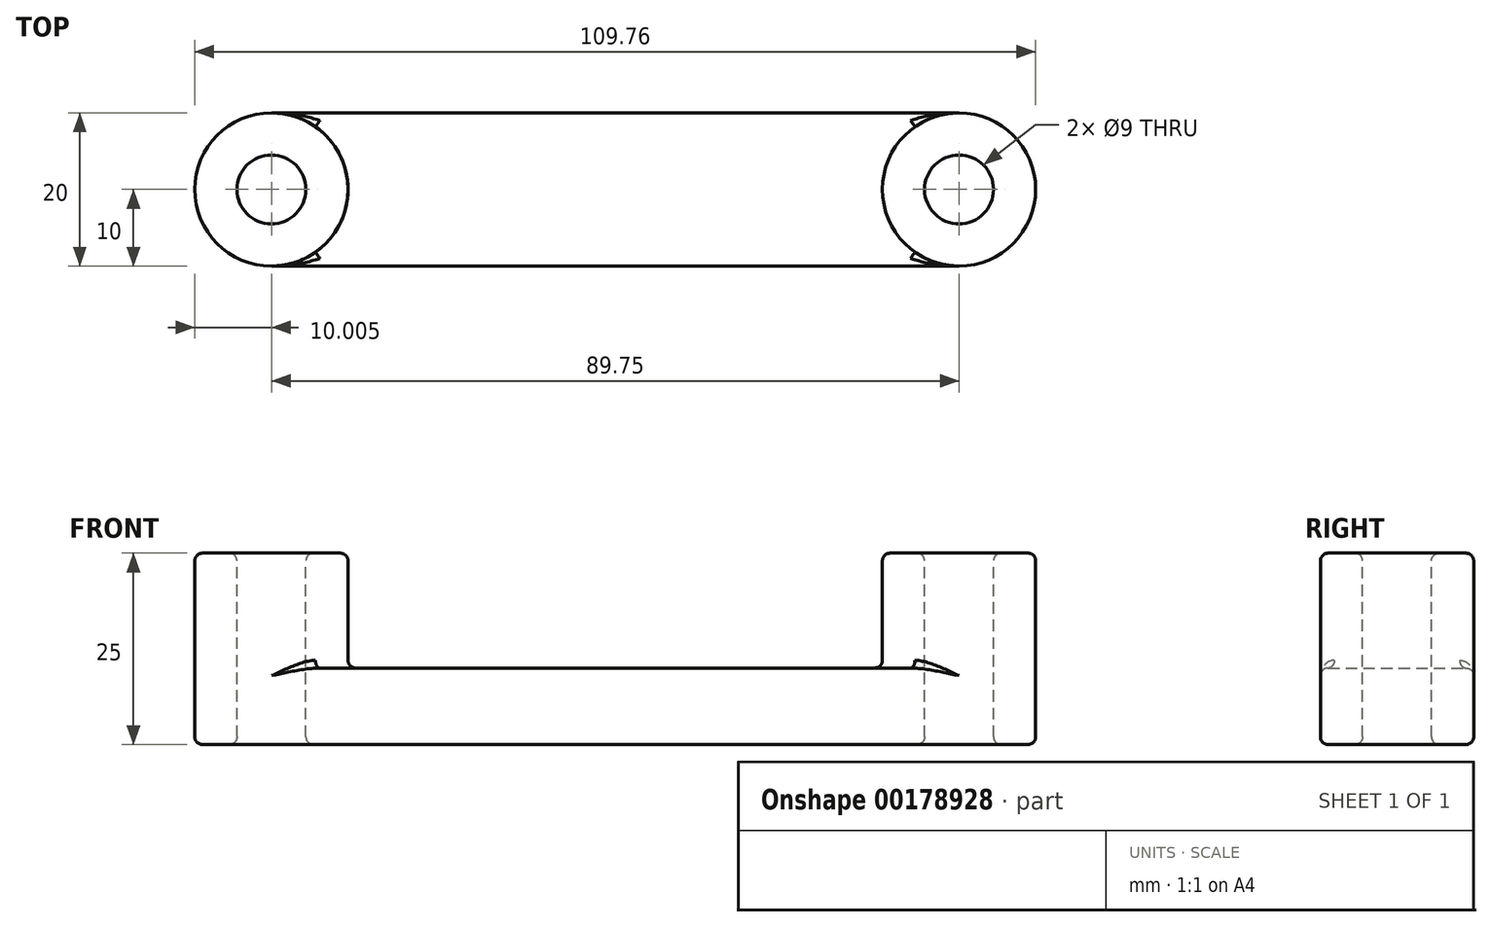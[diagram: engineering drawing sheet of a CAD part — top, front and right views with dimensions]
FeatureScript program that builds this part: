
annotation { "Feature Type Name" : "Feature", "Feature Type Description" : "" }
export const myFeature = defineFeature(function(context is Context, id is Id, definition is map)
    precondition{}
    {
        {
            var Q0;
            Q0=qCreatedBy(makeId("Top.planeOp"),FACE);
            var sketch = newSketch(context, id + "F0", { "sketchPlane" : qUnion([Q0])});
            skLineSegment(sketch, "E0", {"start": v(0, 0) * mm, "end": v(44.88, 0) * mm, "construction": true});
            skLineSegment(sketch, "E1", {"start": v(0, 0) * mm, "end": v(-44.88, 0) * mm, "construction": true});
            skCircle(sketch, "E2", {"center": v(-44.88, 0) * mm, "radius": 4.5 * mm});
            skCircle(sketch, "E3", {"center": v(44.88, 0) * mm, "radius": 4.5 * mm});
            skCircle(sketch, "E4", {"center": v(-44.88, 0) * mm, "radius": 10 * mm});
            skCircle(sketch, "E5", {"center": v(44.88, 0) * mm, "radius": 10 * mm});
            skLineSegment(sketch, "E6", {"start": v(-44.88, 10) * mm, "end": v(44.88, 10) * mm});
            skLineSegment(sketch, "E7", {"start": v(-44.88, -10) * mm, "end": v(44.88, -10) * mm});
            skSolve(sketch);
        }
        {
            var Q0;
            Q0 = qSketchRegion(id + "F0", true);
            extrude(context, id + "F1", {"entities" : qUnion([Q0]), "oppositeDirection" : true, "depth" : 10 * mm});
        }
        {
            var Q0;
            Q0=makeQuery(id+"F0.imprint","IMPRINT",FACE,{"disambiguationData":[TD([[makeQuery(id+"F0.imprint","IMPRINT",EDGE,{"derivedFrom":sQuery(id+"F0.wireOp",EDGE,"E2")}),-1.0]])]});
            var Q1;
            Q1=makeQuery(id+"F0.imprint","IMPRINT",FACE,{"disambiguationData":[TD([[makeQuery(id+"F0.imprint","IMPRINT",EDGE,{"derivedFrom":sQuery(id+"F0.wireOp",EDGE,"E3")}),-1.0]])]});
            extrude(context, id + "F2", {"entities" : qUnion([Q0, Q1]), "operationType" : NewBodyOperationType.ADD, "depth" : 15 * mm});
        }
        {
            var Q0;
            Q0=makeQuery(id+"F2.opExtrude","CAP_FACE",FACE,{"disambiguationData":[OSD([sQuery(id+"F0.wireOp",EDGE,"E2"),sQuery(id+"F0.wireOp",EDGE,"E4")])],"isStart":false});
            var Q1;
            Q1=makeQuery(id+"F1.opExtrude","CAP_FACE",FACE,{"disambiguationData":[OSD([sQuery(id+"F0.wireOp",EDGE,"E2"),sQuery(id+"F0.wireOp",EDGE,"E3"),sQuery(id+"F0.wireOp",EDGE,"E4"),sQuery(id+"F0.wireOp",EDGE,"E5"),sQuery(id+"F0.wireOp",EDGE,"E6"),sQuery(id+"F0.wireOp",EDGE,"E7")])],"isStart":true});
            var Q2;
            Q2=makeQuery(id+"F2.opExtrude","CAP_FACE",FACE,{"disambiguationData":[OSD([sQuery(id+"F0.wireOp",EDGE,"E3"),sQuery(id+"F0.wireOp",EDGE,"E5")])],"isStart":false});
            var Q3;
            Q3=makeQuery(id+"F1.opExtrude","CAP_FACE",FACE,{"disambiguationData":[OSD([sQuery(id+"F0.wireOp",EDGE,"E2"),sQuery(id+"F0.wireOp",EDGE,"E3"),sQuery(id+"F0.wireOp",EDGE,"E4"),sQuery(id+"F0.wireOp",EDGE,"E5"),sQuery(id+"F0.wireOp",EDGE,"E6"),sQuery(id+"F0.wireOp",EDGE,"E7")])],"isStart":false});
            fillet(context, id + "F3", {"entities" : qUnion([Q0, Q1, Q2, Q3]), "radius" : 1 * mm, "tangentPropagation" : true, "allowEdgeOverflow" : false});
        }
    });
